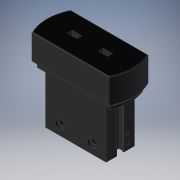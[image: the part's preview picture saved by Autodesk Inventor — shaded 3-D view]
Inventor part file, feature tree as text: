
AUTODESK INVENTOR PART (.ipt)
format: ipt  version: 2019 (Build 230136000, 136)  size: 368,128 bytes
history: native  units: mm
features: other x28, sketch x16, revolve x8, extrude x6, thread x5, hole x2
ambient origin geometry x8: Origin, YZ Plane, XZ Plane, XY Plane, X Axis, Y Axis, Z Axis, Center Point
bodies: Solid1 (feature_tree)
feature tree (65):
  extrude  "Extrusion1"  TaperAngle=360.0deg  [1 undecoded]
  hole  "Hole1"  [1 undecoded]
  hole  "Hole2"  [1 undecoded]
  revolve  "Revolution1"  Angle=360.0deg
  thread  "Thread1"  [1 undecoded]
  extrude  "Extrusion2"  TaperAngle=360.0deg  [1 undecoded]
  extrude  "Extrusion3"  TaperAngle=360.0deg  [1 undecoded]
  revolve  "Revolution2"  [1 undecoded]
  thread  "Thread2"  [1 undecoded]
  revolve  "Revolution3"  [1 undecoded]
  revolve  "Revolution4"  [1 undecoded]
  thread  "Thread3"  [1 undecoded]
  revolve  "Revolution5"  [1 undecoded]
  thread  "Thread4"  [1 undecoded]
  revolve  "Revolution6"  [1 undecoded]
  thread  "Thread5"  [1 undecoded]
  extrude  "Extrusion4"  [1 undecoded]
  revolve  "Revolution7"  [1 undecoded]
  revolve  "Revolution8"  [1 undecoded]
  extrude  "Extrusion5"  [1 undecoded]
  extrude  "Extrusion6"  [1 undecoded]
  other  "JAW_1_XY"
  other  "JAW_1_YZ"
  other  "JAW_1_ZX"
  other  "JAW_1_X"
  other  "JAW_1_Y"
  other  "JAW_1_Z"
  other  "JAW_1_Center"
  other  "JAW_2_XY"
  other  "JAW_2_YZ"
  other  "JAW_2_ZX"
  other  "JAW_2_X"
  other  "JAW_2_Y"
  other  "JAW_2_Z"
  other  "JAW_2_Center"
  other  "ZBH_1_XY"
  other  "ZBH_1_YZ"
  other  "ZBH_1_ZX"
  other  "ZBH_1_X"
  other  "ZBH_1_Y"
  other  "ZBH_1_Z"
  other  "ZBH_1_Center"
  other  "ZBH_2_XY"
  other  "ZBH_2_YZ"
  other  "ZBH_2_ZX"
  other  "ZBH_2_X"
  other  "ZBH_2_Y"
  other  "ZBH_2_Z"
  other  "ZBH_2_Center"
  sketch  "Sketch_1"  dims[d0=22.0mm d1=0.0mm]
  sketch  "Sketch2"  dims[d2=2.459mm d3=3.5mm d4=3.0mm d5=2.0mm d6=90.0deg d7=3.5mm d8=0.0mm]
  sketch  "Sketch3"  dims[d9=2.459mm d10=3.5mm d11=3.0mm d12=2.0mm d13=90.0deg d14=3.5mm d15=0.0mm d16=360.0deg]
  sketch  "Sketch_7"  dims[d39=90.0deg d40=7.5mm d41=0.0mm]
  sketch  "Sketch_8"  dims[d42=7.5mm d43=0.0mm d44=0.0mm d45=0.0mm]
  sketch  "Sketch_9"  dims[d46=0.0mm d47=0.0mm]
  sketch  "Sketch_4"  dims[d21=81.2mm d22=0.0mm d23=360.0deg]
  sketch  "Sketch_14"
  sketch  "Sketch_5"  dims[d28=5.521mm d29=0.0mm d30=360.0deg]
  sketch  "Sketch_15"
  sketch  "Sketch_6"  dims[d34=6.621mm d35=0.0mm d36=67.0mm d37=0.0mm d38=90.0deg]
  sketch  "Skizze_3"  dims[d17=6.621mm d18=0.0mm d19=81.2mm d20=0.0mm]
  sketch  "Skizze_4"  dims[d24=5.521mm d25=0.0mm d26=360.0deg d27=360.0deg]
  sketch  "Skizze_5"  dims[d31=5.521mm d32=0.0mm d33=360.0deg]
  sketch  "Sketch_10"
  sketch  "Sketch_11"
note: 20 required parameter values undecoded (feature->parameter linkage not recoverable at this tier; creation-order binding heuristic only, values carry confidence <= 0.55)